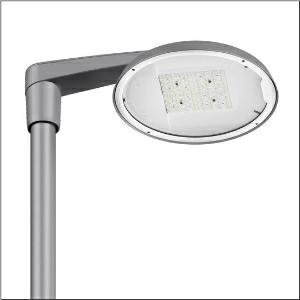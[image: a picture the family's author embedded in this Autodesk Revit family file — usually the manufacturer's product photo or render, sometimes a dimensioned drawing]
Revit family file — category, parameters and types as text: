
# Revit family: dl_r__50_iq_mini___st0_5a_5xa248b41f08ne_73b8
name_source: partatom
category: Lighting Fixtures
units: mm (PartAtom-declared; Revit-internal decimal feet)

## family parameters
Cut with Voids When Loaded = No
Host = Face
Light Source = No
Part Type = Normal
Room Calculation Point = No
Round Connector Dimension = Use Diameter
Shared = No

## types (1)
- --- (1 x LED, 19390 lm, 115.8 W, 4000K)
    Apparent Load = 116 VA
    CIE Flux Codes = 43 76 97 100 100
    Color Rendering = 70
    Color Temperature = 4000K
    Default Elevation = 1800 mm
    Description = DL® 50 iQ mini, mast luminaire, primary light control with lens, of PMMA, primary optical cover: cover, of toughened safety glass, transparent, light distribution: ST0.5a, light emission: direct distribution, primary light characteristic: asymmetric, installation type: side-entry, post-top, LED, High Power LED, rated luminous flux: 19.390lm, luminous efficacy: 167lm/W, light colour: 740, colour temperature: 4000K, control: optimised constant luminous flux control (CLO 2.0), Desk-Remote (wireless, voltage-free reading and setting of iQ features in the workshop via application-optimized NFC function/RFID function), Light-Fading, Smart-Wire, Night-Set, Lumen-Switch, Temp-Guard, Auto-Match, Street-Remote, mains connection: 230..240V, AC, 50/60Hz, connection cable pre-assembled, cable length: 10,5m, start of lifetime: 116W, end of service life: 127W, reduction: 53W, luminaire housing, of diecast aluminium, powder-coated, Siteco® metallic grey (DB 702S), inclination adjustable: 0°, 5°, 10° (post-top) | 0°, -5°, -10°, -15° (side-entry), please order mast post-top element or mast side-entry element separately, diameter: 500mm, height: 115mm, post-top: for spigot size d x l = 76 x 100mm; with reducer (optional accessory) 60 x 100mm | side-entry: for spigot size d x l = 60 x 100mm; with reducer (optional accessory) 42 x 100mm, protection rating (complete): IP66, insulation class (complete): insulation class II (safety insulation), certification: CE, ENEC, VDE, impact resistance: IK08, permissible operating ambient temperature for outdoor applications: -25..+40°C, standard-compliant lighting for roads and squares, packaging unit: 1 piece

Light Distribution: ST0.5a
    Height = 115 mm
    Lamp = 1 x LED
    Lamp Light Flux = 19390 lm
    Lamp Power = 115.8 W
    Lamp count = 1
    Length = 500 mm
    Luminous efficacy = 167 lm/W
    Manufacturer = Siteco
    ModVariant = No
    Model = 5XA248B41F08NE
    Number of Poles = 1
    OnlyDefault = Yes
    Power Factor = 1
    Product Name = DL® 50 iQ mini | ST0.5a
    Product group = mast luminaire | pylon top
    ProductGroupID = 6100
    Protection Class = Protection class II
    Protection Degree = IP 66
    RLX_Detail_Level = 1
    RLX_Emergency_Light_Flux = 0 lm
    RLX_Emergency_Type = 0
    RLX_Emergency_Type_DB = No
    RlxData = <blob elided: 127857 chars, md5=b31ef2e5>
    Socket = socket
    Standby Power = 0 W
    System Light Flux = 19390 lm
    System Power = 116 W
    Type Comments = factory setting: luminous flux: 100 % | dim-lin: 254 | 626 mA
    Type Image = l_1251790.jpg
    URL = http://relux.com
    VarID = @adj_092175
    Voltage = 0 V
    Weight = 0.00 kg
    Width = 0 mm  [stored 0 ft]

note: [stored X ft] marks values corroborated as IEEE doubles in the binary element streams (Revit-internal decimal feet)

## geometry (parser evidence)
native form markers: Blend x4, Sweep x10
no freeform markers — native parametric forms only
